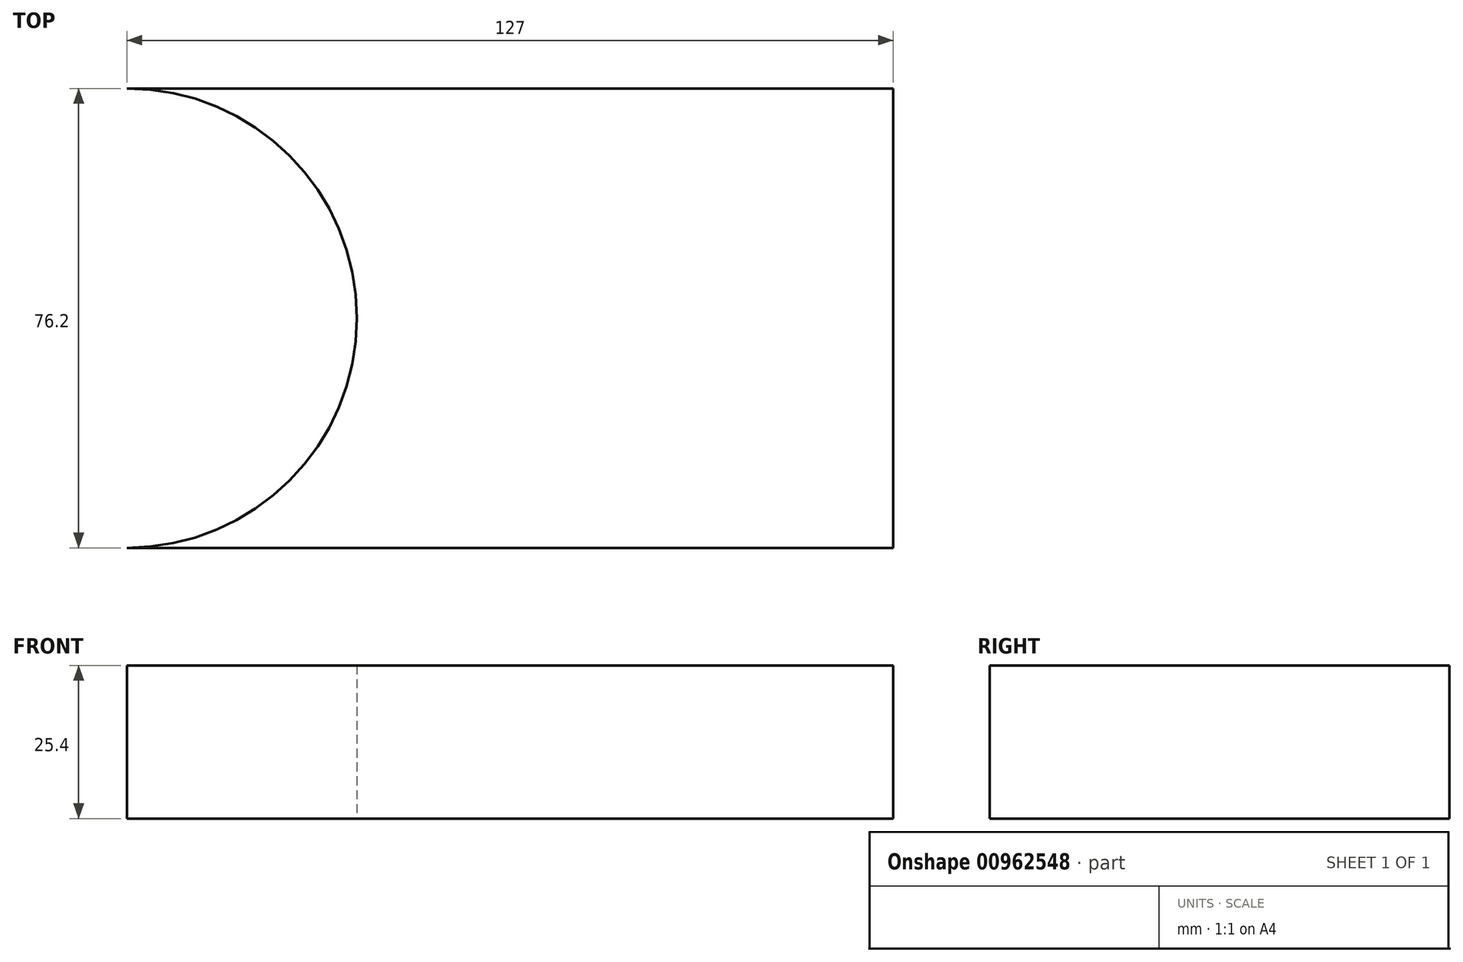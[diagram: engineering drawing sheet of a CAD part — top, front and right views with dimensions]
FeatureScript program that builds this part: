
annotation { "Feature Type Name" : "Feature", "Feature Type Description" : "" }
export const myFeature = defineFeature(function(context is Context, id is Id, definition is map)
    precondition{}
    {
        {
            var Q0;
            Q0=qCreatedBy(makeId("Top.planeOp"),FACE);
            var sketch = newSketch(context, id + "F0", { "sketchPlane" : qUnion([Q0])});
            skLineSegment(sketch, "E0.bottom", {"start": v(63.5, -38.1) * mm, "end": v(-63.5, -38.1) * mm});
            skLineSegment(sketch, "E0.top", {"start": v(63.5, 38.1) * mm, "end": v(-63.5, 38.1) * mm});
            skLineSegment(sketch, "E0.left", {"start": v(63.5, -38.1) * mm, "end": v(63.5, 38.1) * mm});
            skLineSegment(sketch, "E0.right", {"start": v(-63.5, -38.1) * mm, "end": v(-63.5, 38.1) * mm});
            skPoint(sketch, "E0.middle", {"position": v(0, 0) * mm});
            skCircle(sketch, "E1", {"center": v(-63.5, 0) * mm, "radius": 38.1 * mm});
            skCircle(sketch, "E2", {"center": v(-63.5, 0) * mm, "radius": 19.57 * mm});
            skSolve(sketch);
        }
        {
            var Q0;
            {var subQ0=sQuery(id+"F0.wireOp",EDGE,"E2");var subQ1=sQuery(id+"F0.wireOp",EDGE,"E0.right");var subQ2=makeQuery(id+"F0.imprint","INTERSECT",VERTEX,{"disambiguationData":[OD(0.0)],"derivedFrom":[subQ1,subQ0]});Q0=makeQuery(id+"F0.imprint","IMPRINT",FACE,{"disambiguationData":[TD([[makeQuery(id+"F0.imprint","IMPRINT",EDGE,{"disambiguationData":[TD([[subQ2,-1.0]])],"derivedFrom":subQ1}),-1.0]])]});}
            var Q1;
            {var subQ0=sQuery(id+"F0.wireOp",EDGE,"E2");var subQ1=sQuery(id+"F0.wireOp",EDGE,"E0.right");var subQ2=makeQuery(id+"F0.imprint","INTERSECT",VERTEX,{"disambiguationData":[OD(0.0)],"derivedFrom":[subQ1,subQ0]});Q1=makeQuery(id+"F0.imprint","IMPRINT",FACE,{"disambiguationData":[TD([[makeQuery(id+"F0.imprint","IMPRINT",EDGE,{"disambiguationData":[TD([[subQ2,-1.0]])],"derivedFrom":subQ1}),1.0]])]});}
            extrude(context, id + "F1", {"entities" : qUnion([Q0, Q1]), "depth" : 25.4 * mm, "offsetDistance" : 25.4 * mm});
        }
        {
            var Q0;
            Q0 = qSketchRegion(id + "F0", true);
            extrude(context, id + "F2", {"entities" : qUnion([Q0]), "operationType" : NewBodyOperationType.ADD, "depth" : 25.4 * mm, "offsetDistance" : 25.4 * mm});
        }
        {
            var Q0;
            {var subQ0=sQuery(id+"F0.wireOp",EDGE,"E2");var subQ1=sQuery(id+"F0.wireOp",EDGE,"E0.right");var subQ2=makeQuery(id+"F0.imprint","INTERSECT",VERTEX,{"disambiguationData":[OD(0.0)],"derivedFrom":[subQ1,subQ0]});Q0=makeQuery(id+"F0.imprint","IMPRINT",FACE,{"disambiguationData":[TD([[makeQuery(id+"F0.imprint","IMPRINT",EDGE,{"disambiguationData":[TD([[subQ2,-1.0]])],"derivedFrom":subQ1}),1.0]])]});}
            var Q1;
            {var subQ0=sQuery(id+"F0.wireOp",EDGE,"E2");var subQ1=sQuery(id+"F0.wireOp",EDGE,"E0.right");var subQ2=makeQuery(id+"F0.imprint","INTERSECT",VERTEX,{"disambiguationData":[OD(0.0)],"derivedFrom":[subQ1,subQ0]});Q1=makeQuery(id+"F0.imprint","IMPRINT",FACE,{"disambiguationData":[TD([[makeQuery(id+"F0.imprint","IMPRINT",EDGE,{"disambiguationData":[TD([[subQ2,-1.0]])],"derivedFrom":subQ1}),-1.0]])]});}
            extrude(context, id + "F3", {"entities" : qUnion([Q0, Q1]), "operationType" : NewBodyOperationType.REMOVE, "depth" : 25.4 * mm, "offsetDistance" : 25.4 * mm});
        }
    });
